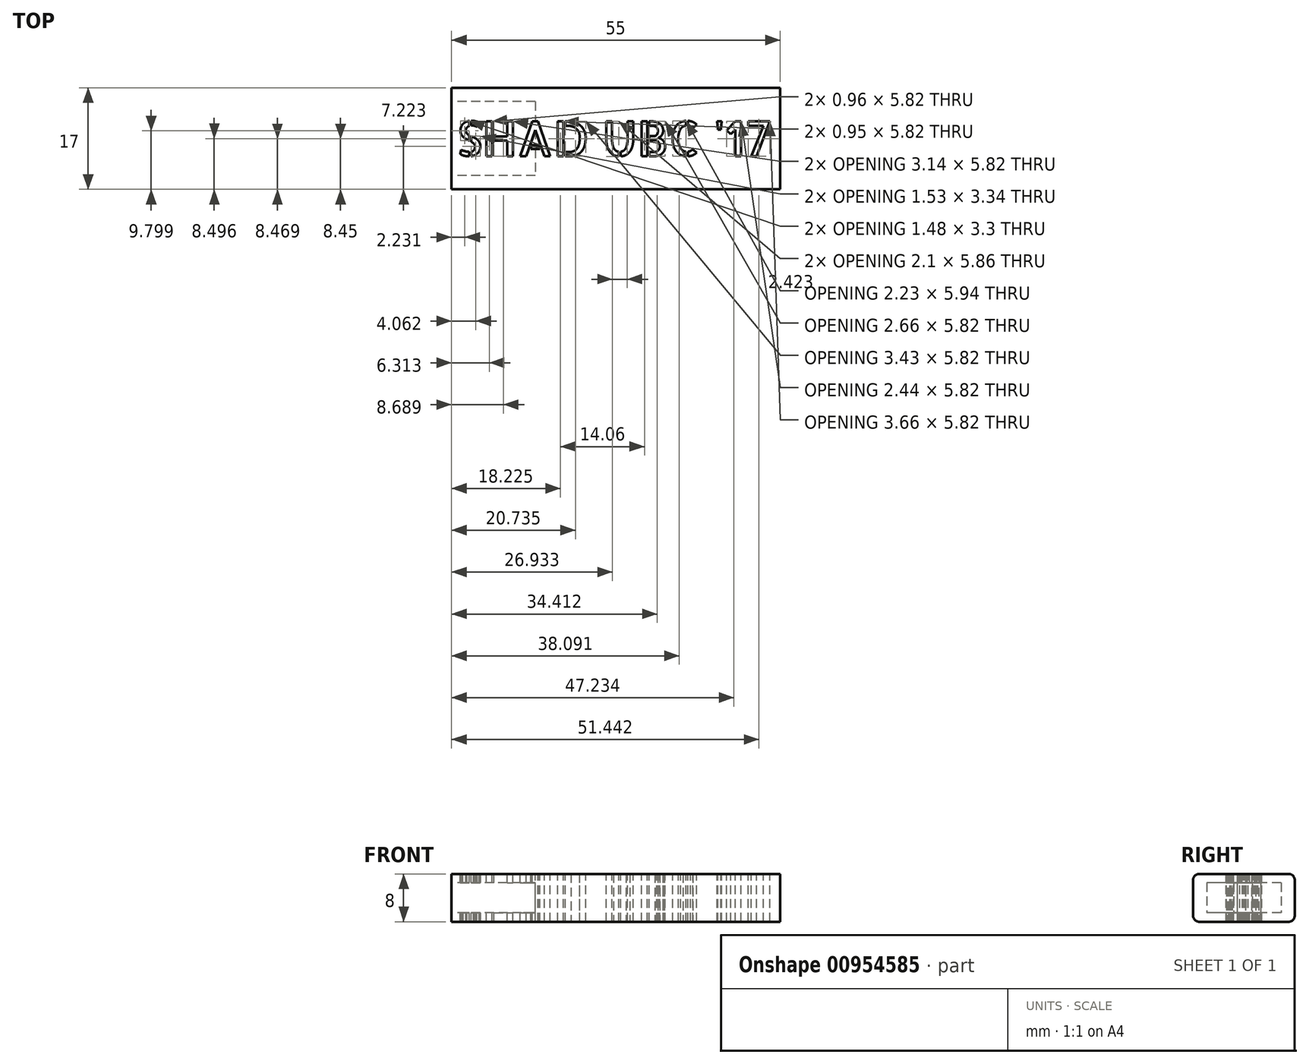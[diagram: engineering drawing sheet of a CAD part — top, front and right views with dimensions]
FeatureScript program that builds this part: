
annotation { "Feature Type Name" : "Feature", "Feature Type Description" : "" }
export const myFeature = defineFeature(function(context is Context, id is Id, definition is map)
    precondition{}
    {
        {
            var Q0;
            Q0=qCreatedBy(makeId("Front.planeOp"),FACE);
            var sketch = newSketch(context, id + "F0", { "sketchPlane" : qUnion([Q0])});
            skLineSegment(sketch, "E0.bottom", {"start": v(-7.5, 4) * mm, "end": v(7.5, 4) * mm});
            skLineSegment(sketch, "E0.top", {"start": v(-7.5, -4) * mm, "end": v(7.5, -4) * mm});
            skLineSegment(sketch, "E0.left", {"start": v(-8.5, 3) * mm, "end": v(-8.5, -3) * mm});
            skLineSegment(sketch, "E0.right", {"start": v(8.5, 3) * mm, "end": v(8.5, -3) * mm});
            skPoint(sketch, "E0.middle", {"position": v(0, 0) * mm});
            skPoint(sketch, "E1.visualSharp", {"position": v(-8.5, 4) * mm});
            skArc(sketch, "E1.filletArc", {"start": v(-7.5, 4) * mm, "mid": v(-8.2, 3.7) * mm, "end": v(-8.5, 3) * mm});
            skPoint(sketch, "E2.visualSharp", {"position": v(-8.5, -4) * mm});
            skArc(sketch, "E2.filletArc", {"start": v(-8.5, -3) * mm, "mid": v(-8.2, -3.7) * mm, "end": v(-7.5, -4) * mm});
            skPoint(sketch, "E3.visualSharp", {"position": v(8.5, 4) * mm});
            skArc(sketch, "E3.filletArc", {"start": v(8.5, 3) * mm, "mid": v(8.2, 3.7) * mm, "end": v(7.5, 4) * mm});
            skPoint(sketch, "E4.visualSharp", {"position": v(8.5, -4) * mm});
            skArc(sketch, "E4.filletArc", {"start": v(7.5, -4) * mm, "mid": v(8.2, -3.7) * mm, "end": v(8.5, -3) * mm});
            skSolve(sketch);
        }
        {
            var Q0;
            Q0 = qSketchRegion(id + "F0", true);
            extrude(context, id + "F1", {"entities" : qUnion([Q0]), "depth" : 55 * mm, "offsetDistance" : 25 * mm});
        }
        {
            var Q0;
            Q0=makeQuery(id+"F1.opExtrude","CAP_FACE",FACE,{"disambiguationData":[OSD([sQuery(id+"F0.wireOp",EDGE,"E0.bottom"),sQuery(id+"F0.wireOp",EDGE,"E0.top"),sQuery(id+"F0.wireOp",EDGE,"E0.left"),sQuery(id+"F0.wireOp",EDGE,"E0.right"),sQuery(id+"F0.wireOp",EDGE,"E1.filletArc"),sQuery(id+"F0.wireOp",EDGE,"E2.filletArc"),sQuery(id+"F0.wireOp",EDGE,"E3.filletArc"),sQuery(id+"F0.wireOp",EDGE,"E4.filletArc")])],"isStart":false});
            var sketch = newSketch(context, id + "F2", { "sketchPlane" : qUnion([Q0])});
            skLineSegment(sketch, "E5.bottom", {"start": v(-6.2, 2.5) * mm, "end": v(6.2, 2.5) * mm});
            skLineSegment(sketch, "E5.top", {"start": v(-6.2, -2.5) * mm, "end": v(6.2, -2.5) * mm});
            skLineSegment(sketch, "E5.left", {"start": v(-6.2, 2.5) * mm, "end": v(-6.2, -2.5) * mm});
            skLineSegment(sketch, "E5.right", {"start": v(6.2, 2.5) * mm, "end": v(6.2, -2.5) * mm});
            skPoint(sketch, "E5.middle", {"position": v(0, 0) * mm});
            skSolve(sketch);
        }
        {
            var Q0;
            Q0 = qSketchRegion(id + "F2", true);
            extrude(context, id + "F3", {"entities" : qUnion([Q0]), "operationType" : NewBodyOperationType.REMOVE, "oppositeDirection" : true, "depth" : 14 * mm, "offsetDistance" : 25 * mm});
        }
        {
            var Q0;
            Q0=makeQuery(id+"F1.opExtrude","SWEPT_BODY",BODY,{"disambiguationData":[OSD([sQuery(id+"F0.wireOp",EDGE,"E0.bottom"),sQuery(id+"F0.wireOp",EDGE,"E0.top"),sQuery(id+"F0.wireOp",EDGE,"E0.left"),sQuery(id+"F0.wireOp",EDGE,"E0.right"),sQuery(id+"F0.wireOp",EDGE,"E1.filletArc"),sQuery(id+"F0.wireOp",EDGE,"E2.filletArc"),sQuery(id+"F0.wireOp",EDGE,"E3.filletArc"),sQuery(id+"F0.wireOp",EDGE,"E4.filletArc")])]});
            var Q1;
            Q1=makeQuery(id+"F1.opExtrude","CAP_EDGE",EDGE,{"disambiguationData":[OSD([sQuery(id+"F0.wireOp",EDGE,"E0.right")])],"isStart":true});
            transform(context, id + "F4", {"entities" : qUnion([Q0]), "transformType" : TransformType.ROTATION, "transformAxis" : qUnion([Q1]), "angle" : 90 * degree, "makeCopy" : false});
        }
        {
            var Q0;
            Q0=makeQuery(id+"F1.opExtrude","SWEPT_FACE",FACE,{"disambiguationData":[OSD([sQuery(id+"F0.wireOp",EDGE,"E0.bottom")])]});
            var sketch = newSketch(context, id + "F5", { "sketchPlane" : qUnion([Q0])});
            skText(sketch, "E6", { "text": "SHAD UBC \'17", "fontName": "AllertaStencil-Regular.ttf"});
            const initialGuessF5  = {"E6": [-0.04569, 0.00556, 1, 0, 0.00582]};
            skSetInitialGuess(sketch, initialGuessF5);
            skSolve(sketch);
        }
        {
            var Q0;
            Q0 = qSketchRegion(id + "F5", true);
            extrude(context, id + "F6", {"entities" : qUnion([Q0]), "operationType" : NewBodyOperationType.REMOVE, "oppositeDirection" : true, "depth" : 8 * mm, "offsetDistance" : 25 * mm});
        }
    });
